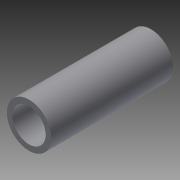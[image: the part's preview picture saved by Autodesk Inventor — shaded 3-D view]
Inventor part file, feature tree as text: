
AUTODESK INVENTOR PART (.ipt)
format: ipt  version: 2015 (Build 190159000, 159)  size: 78,848 bytes
history: native  units: mm
features: extrude x1, sketch x1
ambient origin geometry x8: Origin, YZ Plane, XZ Plane, XY Plane, X Axis, Y Axis, Z Axis, Center Point
bodies: Solid1 (feature_tree)
feature tree (2):
  extrude  "Extrusion1"  Depth=22.0mm
  sketch  "Sketch1"  dims[d0=8.0mm d1=6.0mm d2=22.0mm d3=0.0mm]
